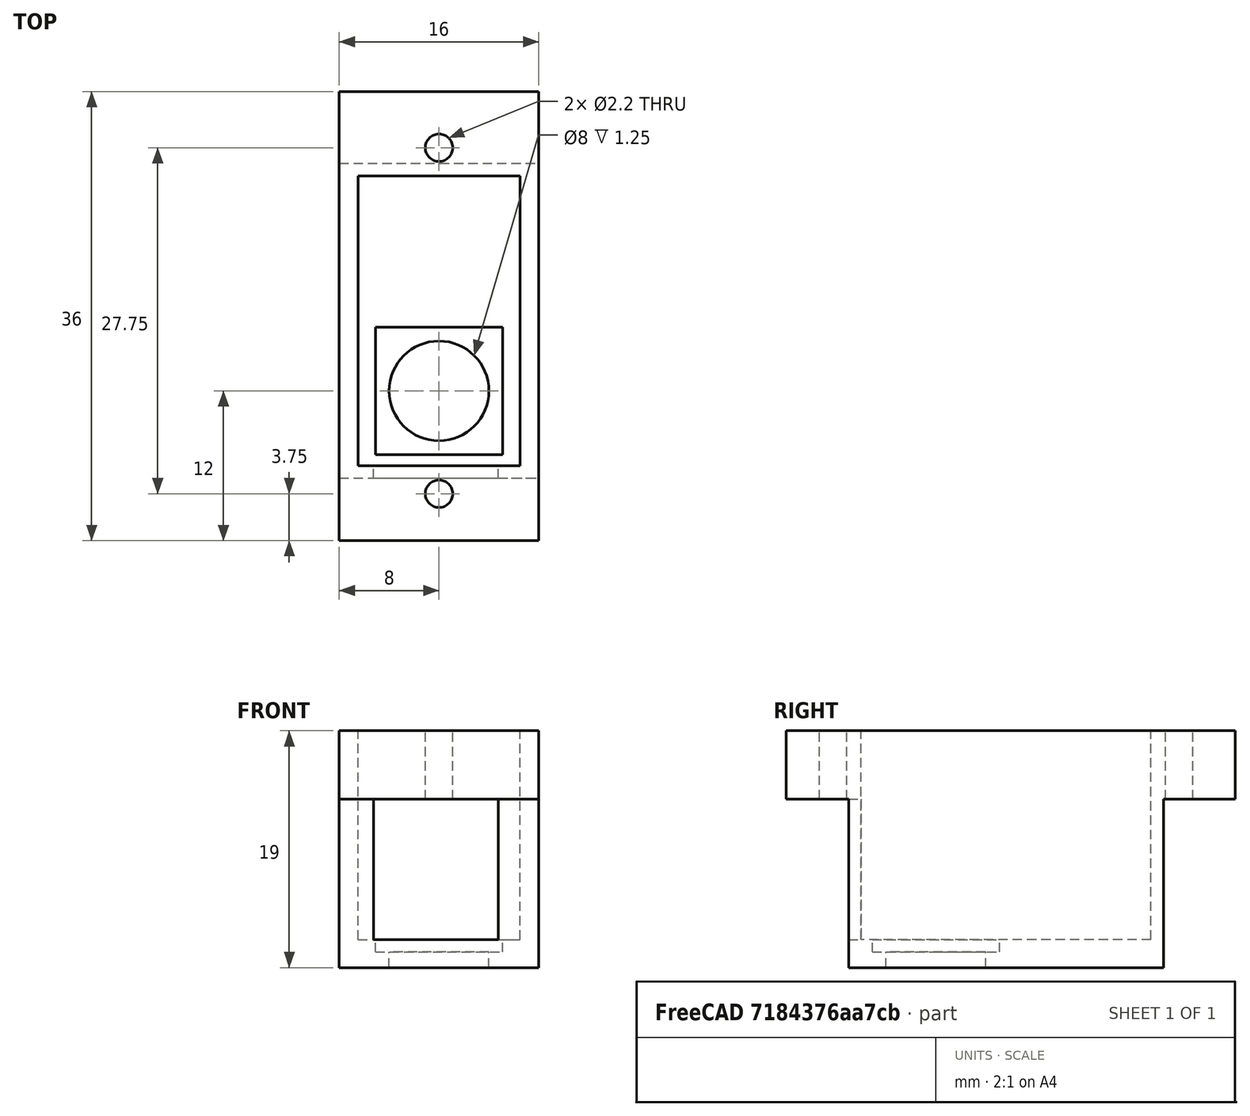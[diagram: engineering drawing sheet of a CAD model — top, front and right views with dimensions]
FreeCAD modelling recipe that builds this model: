
FCSTD DOCUMENT  (FreeCAD 0.18R4 (GitTag))
Label: soporte motor
License: All rights reserved
LicenseURL: http://en.wikipedia.org/wiki/All_rights_reserved
objects: Part::Cut×7, Part::Box×6, Part::Offset×1, Part::Feature×1, Part::Cylinder×1
note: 16 computed .brp shape members not serialized (recipe doc carries the construction recipe); baked Part::Feature solids carry a one-line shape summary decoded from their .brp

FEATURE [Part::Box] Box  label="Cubo"
  AttacherType = Attacher::AttachEngine3D
  Height = 20
  Length = 12.5
  Placement = pos=(0,4.75,0) rot=(0,0,1;0rad)
  Width = 22.75
FEATURE [Part::Box] Box003  label="Cubo003"
  AttacherType = Attacher::AttachEngine3D
  Height = 10
  Length = 18
  Placement = pos=(49,-11,28.75) rot=(0,0,1;0rad)
  Width = 14
FEATURE [Part::Offset] Offset  label="Offset servo"
  Fill = false
  Intersection = false
  Join = 2
  Mode = 0
  Placement = pos=(52,0,0) rot=(1,0,0;1.5708rad)
  SelfIntersection = false
  Source = -> Box
  Value = 0.25
FEATURE [Part::Feature] Part__Feature  label="SG90_servo_con_tornillos"
  Placement = pos=(52,0,0) rot=(1,0,0;1.5708rad)
  shape: bbox 12.5 x 30.45 x 32.25 mm, 42 faces (baked)
FEATURE [Part::Box] Box001  label="Cubo001"
  AttacherType = Attacher::AttachEngine3D
  Height = 36
  Length = 16
  Placement = pos=(50.25,-16.5,-1.5) rot=(0,0,1;0rad)
  Width = 19
FEATURE [Part::Cut] Cut
  Base = -> Box001
  Refine = true
  Tool = -> Part__Feature
FEATURE [Part::Cylinder] Cylinder  label="Cilindro"
  Angle = 360
  AttacherType = Attacher::AttachEngine3D
  Height = 39
  Placement = pos=(58.25,3,10.5) rot=(1,0,0;1.5708rad)
  Radius = 4
FEATURE [Part::Cut] Cut001
  Base = -> Cut
  Refine = true
  Tool = -> Cylinder
FEATURE [Part::Cut] Cut006
  Base = -> Cut001
  Refine = true
  Tool = -> Offset
FEATURE [Part::Box] Box002  label="Cubo002"
  AttacherType = Attacher::AttachEngine3D
  Height = 10.5
  Length = 18
  Placement = pos=(49,-11,-7) rot=(0,0,1;0rad)
  Width = 14
FEATURE [Part::Cut] Cut007
  Base = -> Cut006
  Refine = true
  Tool = -> Box002
FEATURE [Part::Cut] Cut008  label="soporte motor sin agujero"
  Base = -> Cut007
  Placement = pos=(-50,1,0) rot=(-1,0,0;1.5708rad)
  Refine = true
  Tool = -> Box003
FEATURE [Part::Box] Box004  label="Cubo004"
  AttacherType = Attacher::AttachEngine3D
  Height = 11.25
  Length = 10
  Placement = pos=(3,0,-0.25) rot=(0,0,1;0rad)
  Width = 10
FEATURE [Part::Cut] Cut009  label="soporte motor agujereado"
  Base = -> Cut008
  Refine = true
  Tool = -> Box004
FEATURE [Part::Box] Box005  label="hueco tapon"
  AttacherType = Attacher::AttachEngine3D
  Height = 1
  Length = 10.2
  Placement = pos=(3.15,6.4,-1.25) rot=(0,0,1;0rad)
  Width = 10.2
FEATURE [Part::Cut] Cut010  label="soporte motor con hueco tapon"
  Base = -> Cut009
  Refine = true
  Tool = -> Box005
